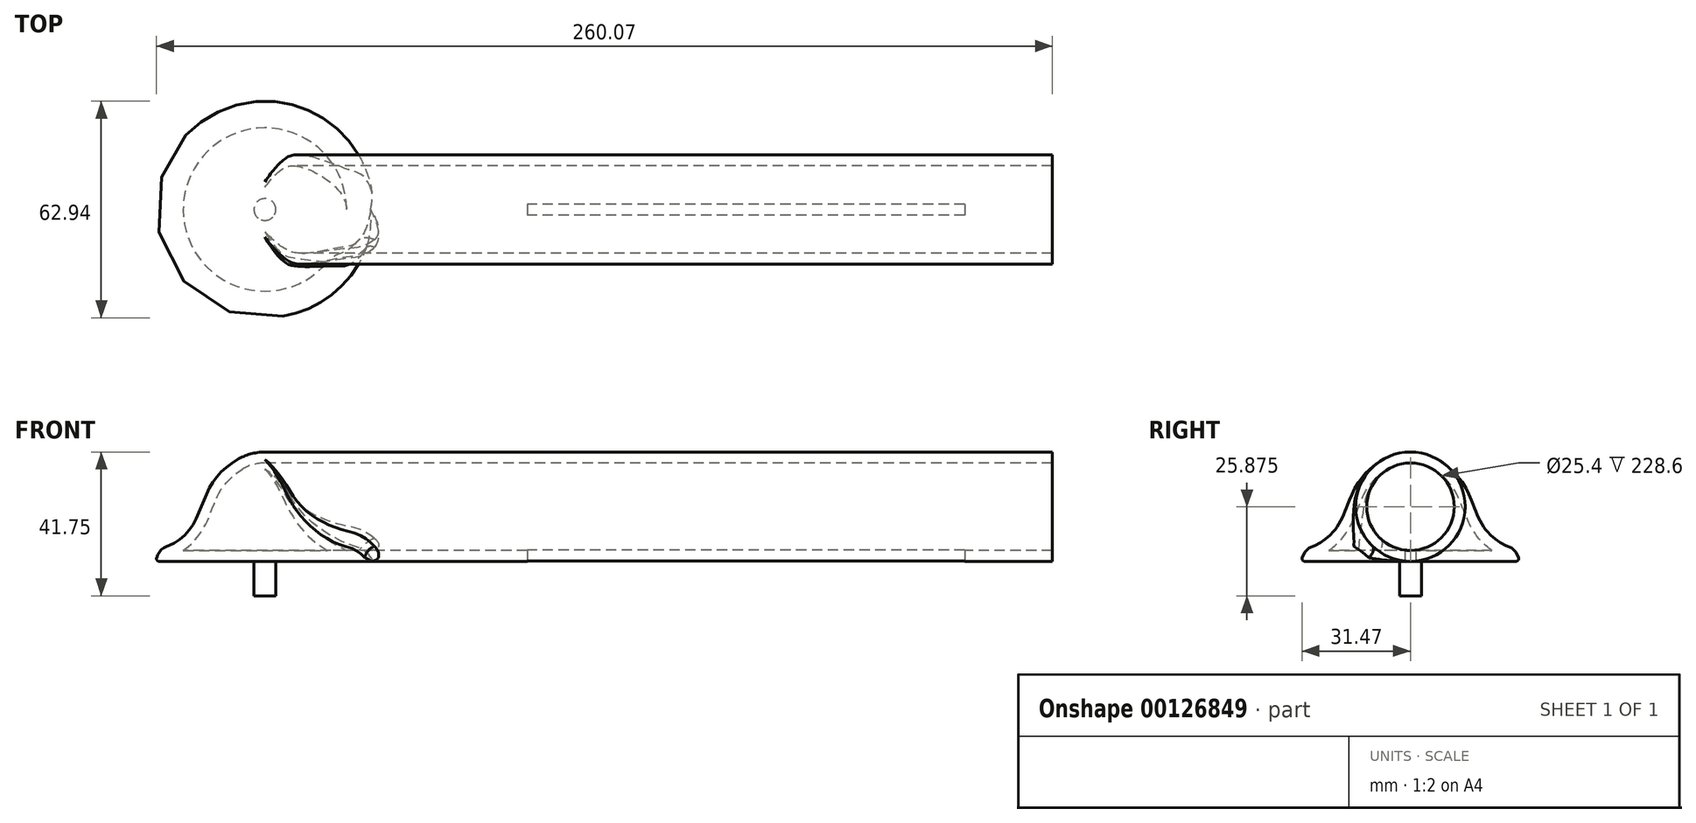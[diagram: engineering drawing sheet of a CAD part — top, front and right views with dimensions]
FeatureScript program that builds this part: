
annotation { "Feature Type Name" : "Feature", "Feature Type Description" : "" }
export const myFeature = defineFeature(function(context is Context, id is Id, definition is map)
    precondition{}
    {
        {
            var Q0;
            Q0=qCreatedBy(makeId("Front.planeOp"),FACE);
            var sketch = newSketch(context, id + "F0", { "sketchPlane" : qUnion([Q0])});
            skLineSegment(sketch, "E0", {"start": v(228.6, 0) * mm, "end": v(-31.75, 0) * mm});
            skLineSegment(sketch, "E1.bottom", {"start": v(-8.06, 31.75) * mm, "end": v(228.6, 31.75) * mm});
            skLineSegment(sketch, "E1.left", {"start": v(-8.06, 31.75) * mm, "end": v(-8.06, 0) * mm});
            skLineSegment(sketch, "E1.right", {"start": v(228.6, 31.75) * mm, "end": v(228.6, 0) * mm});
            skLineSegment(sketch, "E2", {"start": v(-8.06, 15.87) * mm, "end": v(228.6, 15.87) * mm});
            skArc(sketch, "E3", {"start": v(0, 31.75) * mm, "mid": v(-4.18, 31.2) * mm, "end": v(-8.06, 29.55) * mm});
            skFitSpline(sketch, "E4", {"points": [v(-31.75, 0) * mm, v(-27.3, 4.8) * mm, v(-20.89, 10.66) * mm, v(-16.08, 21.36) * mm, v(-8.06, 29.55) * mm], "startDerivative": vector(16.83, 61.26) * mm, "endDerivative": vector(37.3, 22) * mm});
            skPoint(sketch, "E5.orphan", {"position": v(-15.88, 15.88) * mm});
            skLineSegment(sketch, "E6", {"start": v(0, 31.75) * mm, "end": v(0, 0) * mm});
            skSolve(sketch);
        }
        {
            var Q0;
            {var subQ0=sQuery(id+"F0.wireOp",EDGE,"E4");Q0=makeQuery(id+"F0.imprint","IMPRINT",FACE,{"disambiguationData":[TD([[makeQuery(id+"F0.imprint","IMPRINT",EDGE,{"derivedFrom":subQ0}),-1.0]])]});}
            var Q1;
            {var subQ0=sQuery(id+"F0.wireOp",EDGE,"E2");var subQ1=sQuery(id+"F0.wireOp",EDGE,"E1.left");var subQ2=makeQuery(id+"F0.imprint","INTERSECT",VERTEX,{"derivedFrom":[subQ1,subQ0]});Q1=makeQuery(id+"F0.imprint","IMPRINT",FACE,{"disambiguationData":[TD([[makeQuery(id+"F0.imprint","IMPRINT",EDGE,{"disambiguationData":[TD([[subQ2,1.0]])],"derivedFrom":subQ1}),1.0]])]});}
            var Q2;
            {var subQ0=sQuery(id+"F0.wireOp",EDGE,"E1.left");var subQ1=sQuery(id+"F0.wireOp",EDGE,"E0");var subQ2=makeQuery(id+"F0.imprint","INTERSECT",VERTEX,{"derivedFrom":[subQ1,subQ0]});Q2=makeQuery(id+"F0.imprint","IMPRINT",FACE,{"disambiguationData":[TD([[makeQuery(id+"F0.imprint","IMPRINT",EDGE,{"disambiguationData":[TD([[subQ2,1.0]])],"derivedFrom":subQ1}),-1.0]])]});}
            var Q3;
            Q3=sQuery(id+"F0.wireOp",EDGE,"E6");
            revolve(context, id + "F1", {"entities" : qUnion([Q0, Q1, Q2]), "axis" : qUnion([Q3]), "revolveType" : RevolveType.FULL});
        }
        {
            var Q0;
            Q0=makeQuery(id+"F1.opRevolve","SWEPT_EDGE",EDGE,{"disambiguationData":[OSD([sQuery(id+"F0.wireOp",EDGE,"E0"),sQuery(id+"F0.wireOp",EDGE,"E4")])]});
            fillet(context, id + "F2", {"entities" : qUnion([Q0]), "radius" : 0.8 * mm, "tangentPropagation" : true, "allowEdgeOverflow" : false});
        }
        {
            var Q0;
            {var subQ0=sQuery(id+"F0.wireOp",EDGE,"E1.right");var subQ1=sQuery(id+"F0.wireOp",EDGE,"E1.bottom");var subQ2=makeQuery(id+"F0.imprint","INTERSECT",VERTEX,{"derivedFrom":[subQ1,subQ0]});Q0=makeQuery(id+"F0.imprint","IMPRINT",FACE,{"disambiguationData":[TD([[makeQuery(id+"F0.imprint","IMPRINT",EDGE,{"disambiguationData":[TD([[subQ2,-1.0]])],"derivedFrom":subQ0}),-1.0]])]});}
            var Q1;
            Q1=sQuery(id+"F0.wireOp",EDGE,"E2");
            revolve(context, id + "F3", {"operationType" : NewBodyOperationType.ADD, "entities" : qUnion([Q0]), "axis" : qUnion([Q1]), "revolveType" : RevolveType.FULL});
        }
        {
            var Q0;
            Q0=makeQuery(id+"F3.boolean.opBoolean","INTERSECT",EDGE,{"disambiguationData":[OD(0.0)],"derivedFrom":[makeQuery(id+"F1.opRevolve","SWEPT_FACE",FACE,{"disambiguationData":[OSD([sQuery(id+"F0.wireOp",EDGE,"E4")])]}),makeQuery(id+"F3.opRevolve","SWEPT_FACE",FACE,{"disambiguationData":[OSD([sQuery(id+"F0.wireOp",EDGE,"E1.bottom")])]})]});
            fillet(context, id + "F4", {"entities" : qUnion([Q0]), "radius" : 3.17 * mm, "tangentPropagation" : true, "allowEdgeOverflow" : false});
        }
        {
            var Q0;
            Q0=makeQuery(id+"F1.opRevolve","SWEPT_FACE",FACE,{"disambiguationData":[OSD([sQuery(id+"F0.wireOp",EDGE,"E0"),sQuery(id+"F0.wireOp",EDGE,"E1.top")])]});
            var sketch = newSketch(context, id + "F5", { "sketchPlane" : qUnion([Q0])});
            skCircle(sketch, "E7", {"center": v(0, 0) * mm, "radius": 3.18 * mm});
            skSolve(sketch);
        }
        {
            var Q0;
            Q0 = qSketchRegion(id + "F5", true);
            extrude(context, id + "F6", {"entities" : qUnion([Q0]), "operationType" : NewBodyOperationType.ADD, "depth" : 10 * mm});
        }
        {
            var Q0;
            Q0=makeQuery(id+"F3.opRevolve","SWEPT_FACE",FACE,{"disambiguationData":[OSD([sQuery(id+"F0.wireOp",EDGE,"E1.right")])]});
            shell(context, id + "F7", {"entities" : qUnion([Q0]), "thickness" : 3.17 * mm});
        }
        {
            var Q0;
            Q0=makeQuery(id+"F1.opRevolve","SWEPT_FACE",FACE,{"disambiguationData":[OSD([sQuery(id+"F0.wireOp",EDGE,"E0"),sQuery(id+"F0.wireOp",EDGE,"E1.top")])]});
            var sketch = newSketch(context, id + "F8", { "sketchPlane" : qUnion([Q0])});
            skLineSegment(sketch, "E8", {"start": v(76.2, 0) * mm, "end": v(203.2, 0) * mm, "construction": true});
            skLineSegment(sketch, "E9.0.left", {"start": v(76.2, 1.59) * mm, "end": v(203.2, 1.59) * mm});
            skLineSegment(sketch, "E9.0.right", {"start": v(76.2, -1.59) * mm, "end": v(203.2, -1.59) * mm});
            skPoint(sketch, "E10", {"position": v(0, 0) * mm});
            skLineSegment(sketch, "E11", {"start": v(76.2, 1.59) * mm, "end": v(76.2, -1.59) * mm});
            skLineSegment(sketch, "E12", {"start": v(203.2, 1.59) * mm, "end": v(203.2, -1.59) * mm});
            skSolve(sketch);
        }
        {
            var Q0;
            Q0 = qSketchRegion(id + "F8", true);
            extrude(context, id + "F9", {"entities" : qUnion([Q0]), "operationType" : NewBodyOperationType.REMOVE, "oppositeDirection" : true, "depth" : 17.08 * mm});
        }
    });
